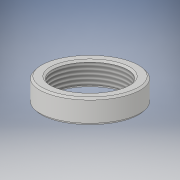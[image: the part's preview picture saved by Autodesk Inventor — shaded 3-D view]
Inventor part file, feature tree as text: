
AUTODESK INVENTOR PART (.ipt)
format: ipt  version: 2018 (Build 220112000, 112)  size: 131,584 bytes
history: native  units: mm
features: revolve x1, thread x1, sketch x1
ambient origin geometry x8: Origin, YZ Plane, XZ Plane, XY Plane, X Axis, Y Axis, Z Axis, Center Point
bodies: Solid1 (feature_tree)
feature tree (3):
  revolve  "Revolution1"  [1 undecoded]
  thread  "Thread1"  [1 undecoded]
  sketch  "Sketch1"  dims[d3=3.0mm d4=4.5mm d6=6.0mm d7=0.25mm d8=0.25mm d9=0.25mm d10=0.25mm d11=0.25mm d12=0.25mm d13=0.25mm d14=0.25mm d15=90.0deg d16=10.0mm d17=0.0mm]
note: 2 required parameter values undecoded (feature->parameter linkage not recoverable at this tier; creation-order binding heuristic only, values carry confidence <= 0.55)